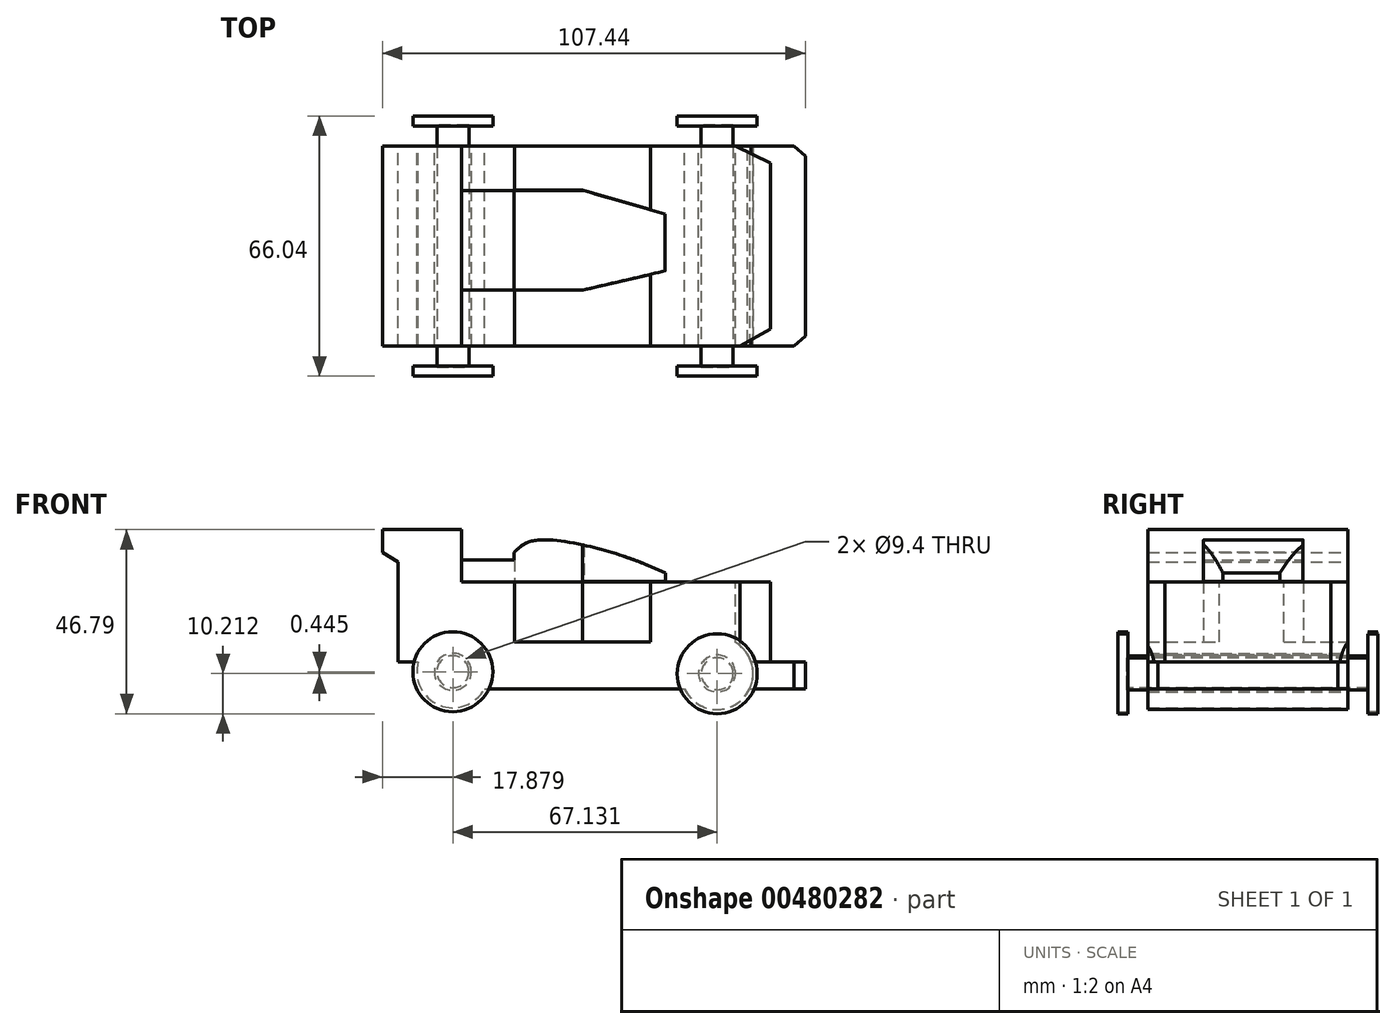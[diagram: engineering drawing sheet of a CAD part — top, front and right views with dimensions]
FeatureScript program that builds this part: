
annotation { "Feature Type Name" : "Feature", "Feature Type Description" : "" }
export const myFeature = defineFeature(function(context is Context, id is Id, definition is map)
    precondition{}
    {
        {
            var Q0;
            Q0=qCreatedBy(makeId("Front.planeOp"),FACE);
            var sketch = newSketch(context, id + "F0", { "sketchPlane" : qUnion([Q0])});
            skCircle(sketch, "E0", {"center": v(-30.53, -30.3) * mm, "radius": 9.14 * mm});
            skPoint(sketch, "E0.first.point", {"position": v(-22.47, -34.62) * mm});
            skPoint(sketch, "E0.second.point", {"position": v(-38.95, -26.72) * mm});
            skPoint(sketch, "E0.third.point", {"position": v(-21.57, -28.46) * mm});
            skCircle(sketch, "E1", {"center": v(36.63, -30.8) * mm, "radius": 9.14 * mm});
            skPoint(sketch, "E1.first.point", {"position": v(27.8, -28.46) * mm});
            skPoint(sketch, "E1.second.point", {"position": v(45.48, -28.46) * mm});
            skPoint(sketch, "E1.third.point", {"position": v(44.94, -34.62) * mm});
            skLineSegment(sketch, "E2", {"start": v(-22.47, -34.62) * mm, "end": v(28.33, -34.62) * mm});
            skLineSegment(sketch, "E3", {"start": v(44.94, -34.62) * mm, "end": v(59.03, -34.62) * mm});
            skLineSegment(sketch, "E4", {"start": v(59.03, -34.62) * mm, "end": v(59.03, -27.76) * mm});
            skLineSegment(sketch, "E5", {"start": v(59.03, -27.76) * mm, "end": v(50.14, -27.76) * mm});
            skLineSegment(sketch, "E6", {"start": v(50.14, -27.76) * mm, "end": v(50.14, -7.44) * mm});
            skLineSegment(sketch, "E7", {"start": v(50.14, -7.44) * mm, "end": v(19.66, -7.44) * mm});
            skLineSegment(sketch, "E8", {"start": v(19.66, -7.44) * mm, "end": v(19.66, -22.68) * mm});
            skLineSegment(sketch, "E9", {"start": v(19.66, -22.68) * mm, "end": v(-14.88, -22.68) * mm});
            skLineSegment(sketch, "E10", {"start": v(-14.88, -22.68) * mm, "end": v(-14.88, -7.44) * mm});
            skLineSegment(sketch, "E11", {"start": v(-14.88, -7.44) * mm, "end": v(-28.34, -7.44) * mm});
            skLineSegment(sketch, "E12", {"start": v(-28.34, -7.44) * mm, "end": v(-28.34, 5.84) * mm});
            skLineSegment(sketch, "E13", {"start": v(-28.34, 5.84) * mm, "end": v(-48.4, 5.84) * mm});
            skLineSegment(sketch, "E14", {"start": v(-48.4, 5.84) * mm, "end": v(-48.4, 0) * mm});
            skLineSegment(sketch, "E15", {"start": v(-48.4, 0) * mm, "end": v(-44.43, -2.36) * mm});
            skLineSegment(sketch, "E16", {"start": v(-44.43, -2.36) * mm, "end": v(-44.43, -27.76) * mm});
            skLineSegment(sketch, "E17", {"start": v(-44.43, -27.76) * mm, "end": v(-38.95, -27.76) * mm});
            skSolve(sketch);
        }
        {
            var Q0;
            Q0=qSketchRegion(id+"F0",true);
            extrude(context, id + "F1", {"entities" : qUnion([Q0]), "depth" : 50.8 * mm});
        }
        {
            var Q0;
            Q0=makeQuery(id+"F1.opExtrude","CAP_FACE",FACE,{"disambiguationData":[OSD([sQuery(id+"F0.wireOp",EDGE,"E0"),sQuery(id+"F0.wireOp",EDGE,"E1"),sQuery(id+"F0.wireOp",EDGE,"E2"),sQuery(id+"F0.wireOp",EDGE,"E3"),sQuery(id+"F0.wireOp",EDGE,"E4"),sQuery(id+"F0.wireOp",EDGE,"E5"),sQuery(id+"F0.wireOp",EDGE,"E6"),sQuery(id+"F0.wireOp",EDGE,"E7"),sQuery(id+"F0.wireOp",EDGE,"E8"),sQuery(id+"F0.wireOp",EDGE,"E9"),sQuery(id+"F0.wireOp",EDGE,"E10"),sQuery(id+"F0.wireOp",EDGE,"E11"),sQuery(id+"F0.wireOp",EDGE,"E12"),sQuery(id+"F0.wireOp",EDGE,"E13"),sQuery(id+"F0.wireOp",EDGE,"E14"),sQuery(id+"F0.wireOp",EDGE,"E15"),sQuery(id+"F0.wireOp",EDGE,"E16"),sQuery(id+"F0.wireOp",EDGE,"E17")])],"isStart":false});
            var sketch = newSketch(context, id + "F2", { "sketchPlane" : qUnion([Q0])});
            skCircle(sketch, "E18", {"center": v(-30.53, -30.3) * mm, "radius": 9.14 * mm});
            skCircle(sketch, "E19", {"center": v(36.63, -30.8) * mm, "radius": 9.14 * mm});
            skSolve(sketch);
        }
        {
            var Q0;
            Q0=qSketchRegion(id+"F2",true);
            extrude(context, id + "F3", {"entities" : qUnion([Q0]), "operationType" : NewBodyOperationType.REMOVE, "oppositeDirection" : true, "depth" : 54.86 * mm});
        }
        {
            var Q0;
            Q0=makeQuery(id+"F1.opExtrude","CAP_FACE",FACE,{"disambiguationData":[OSD([sQuery(id+"F0.wireOp",EDGE,"E0"),sQuery(id+"F0.wireOp",EDGE,"E1"),sQuery(id+"F0.wireOp",EDGE,"E2"),sQuery(id+"F0.wireOp",EDGE,"E3"),sQuery(id+"F0.wireOp",EDGE,"E4"),sQuery(id+"F0.wireOp",EDGE,"E5"),sQuery(id+"F0.wireOp",EDGE,"E6"),sQuery(id+"F0.wireOp",EDGE,"E7"),sQuery(id+"F0.wireOp",EDGE,"E8"),sQuery(id+"F0.wireOp",EDGE,"E9"),sQuery(id+"F0.wireOp",EDGE,"E10"),sQuery(id+"F0.wireOp",EDGE,"E11"),sQuery(id+"F0.wireOp",EDGE,"E12"),sQuery(id+"F0.wireOp",EDGE,"E13"),sQuery(id+"F0.wireOp",EDGE,"E14"),sQuery(id+"F0.wireOp",EDGE,"E15"),sQuery(id+"F0.wireOp",EDGE,"E16"),sQuery(id+"F0.wireOp",EDGE,"E17")])],"isStart":false});
            var sketch = newSketch(context, id + "F4", { "sketchPlane" : qUnion([Q0])});
            skCircle(sketch, "E20", {"center": v(36.63, -30.8) * mm, "radius": 4.06 * mm});
            skCircle(sketch, "E21", {"center": v(-30.53, -30.3) * mm, "radius": 4.06 * mm});
            skSolve(sketch);
        }
        {
            var Q0;
            Q0=qSketchRegion(id+"F4",true);
            extrude(context, id + "F5", {"entities" : qUnion([Q0]), "oppositeDirection" : true, "depth" : 56.13 * mm, "hasSecondDirection" : true, "secondDirectionOppositeDirection" : false, "secondDirectionDepth" : 5.33 * mm});
        }
        {
            var Q0;
            Q0=makeQuery(id+"F1.opExtrude","CAP_FACE",FACE,{"disambiguationData":[OSD([sQuery(id+"F0.wireOp",EDGE,"E0"),sQuery(id+"F0.wireOp",EDGE,"E1"),sQuery(id+"F0.wireOp",EDGE,"E2"),sQuery(id+"F0.wireOp",EDGE,"E3"),sQuery(id+"F0.wireOp",EDGE,"E4"),sQuery(id+"F0.wireOp",EDGE,"E5"),sQuery(id+"F0.wireOp",EDGE,"E6"),sQuery(id+"F0.wireOp",EDGE,"E7"),sQuery(id+"F0.wireOp",EDGE,"E8"),sQuery(id+"F0.wireOp",EDGE,"E9"),sQuery(id+"F0.wireOp",EDGE,"E10"),sQuery(id+"F0.wireOp",EDGE,"E11"),sQuery(id+"F0.wireOp",EDGE,"E12"),sQuery(id+"F0.wireOp",EDGE,"E13"),sQuery(id+"F0.wireOp",EDGE,"E14"),sQuery(id+"F0.wireOp",EDGE,"E15"),sQuery(id+"F0.wireOp",EDGE,"E16"),sQuery(id+"F0.wireOp",EDGE,"E17")])],"isStart":false});
            var sketch = newSketch(context, id + "F6", { "sketchPlane" : qUnion([Q0])});
            skCircle(sketch, "E22", {"center": v(-30.53, -30.3) * mm, "radius": 10.16 * mm});
            skCircle(sketch, "E23", {"center": v(36.63, -30.8) * mm, "radius": 10.16 * mm});
            skSolve(sketch);
        }
        {
            var Q0;
            Q0=qSketchRegion(id+"F6",true);
            extrude(context, id + "F7", {"entities" : qUnion([Q0]), "depth" : 7.62 * mm, "hasSecondDirection" : true, "secondDirectionOppositeDirection" : false, "secondDirectionDepth" : 5.08 * mm});
        }
        {
            var Q0;
            Q0=makeQuery(id+"F1.opExtrude","CAP_FACE",FACE,{"disambiguationData":[OSD([sQuery(id+"F0.wireOp",EDGE,"E0"),sQuery(id+"F0.wireOp",EDGE,"E1"),sQuery(id+"F0.wireOp",EDGE,"E2"),sQuery(id+"F0.wireOp",EDGE,"E3"),sQuery(id+"F0.wireOp",EDGE,"E4"),sQuery(id+"F0.wireOp",EDGE,"E5"),sQuery(id+"F0.wireOp",EDGE,"E6"),sQuery(id+"F0.wireOp",EDGE,"E7"),sQuery(id+"F0.wireOp",EDGE,"E8"),sQuery(id+"F0.wireOp",EDGE,"E9"),sQuery(id+"F0.wireOp",EDGE,"E10"),sQuery(id+"F0.wireOp",EDGE,"E11"),sQuery(id+"F0.wireOp",EDGE,"E12"),sQuery(id+"F0.wireOp",EDGE,"E13"),sQuery(id+"F0.wireOp",EDGE,"E14"),sQuery(id+"F0.wireOp",EDGE,"E15"),sQuery(id+"F0.wireOp",EDGE,"E16"),sQuery(id+"F0.wireOp",EDGE,"E17")])],"isStart":true});
            var sketch = newSketch(context, id + "F8", { "sketchPlane" : qUnion([Q0])});
            skCircle(sketch, "E24", {"center": v(-36.63, -30.8) * mm, "radius": 10.16 * mm});
            skCircle(sketch, "E25", {"center": v(30.53, -30.3) * mm, "radius": 10.16 * mm});
            skSolve(sketch);
        }
        {
            var Q0;
            Q0=qSketchRegion(id+"F8",true);
            extrude(context, id + "F9", {"entities" : qUnion([Q0]), "depth" : 7.62 * mm, "hasSecondDirection" : true, "secondDirectionOppositeDirection" : false, "secondDirectionDepth" : 5.08 * mm});
        }
        {
            var Q0;
            Q0=makeQuery(id+"F1.opExtrude","SWEPT_FACE",FACE,{"disambiguationData":[OSD([sQuery(id+"F0.wireOp",EDGE,"E9")])]});
            var sketch = newSketch(context, id + "F10", { "sketchPlane" : qUnion([Q0])});
            skLineSegment(sketch, "E26.bottom", {"start": v(-14.88, -11.2) * mm, "end": v(19.66, -11.2) * mm});
            skLineSegment(sketch, "E26.top", {"start": v(-14.88, -36.6) * mm, "end": v(19.66, -36.6) * mm});
            skLineSegment(sketch, "E26.left", {"start": v(-14.88, -11.2) * mm, "end": v(-14.88, -36.6) * mm});
            skLineSegment(sketch, "E26.right", {"start": v(19.66, -11.2) * mm, "end": v(19.66, -36.6) * mm});
            skSolve(sketch);
        }
        {
            var Q0;
            Q0=qSketchRegion(id+"F10",true);
            extrude(context, id + "F11", {"entities" : qUnion([Q0]), "operationType" : NewBodyOperationType.ADD, "depth" : 15.24 * mm});
        }
        {
            var Q0;
            Q0=makeQuery(id+"F11.boolean.opBoolean","MERGE",FACE,{"derivedFrom":[makeQuery(id+"F1.opExtrude","SWEPT_FACE",FACE,{"disambiguationData":[OSD([sQuery(id+"F0.wireOp",EDGE,"E7")])]}),makeQuery(id+"F1.opExtrude","SWEPT_FACE",FACE,{"disambiguationData":[OSD([sQuery(id+"F0.wireOp",EDGE,"E11")])]}),makeQuery(id+"F11.opExtrude","CAP_FACE",FACE,{"disambiguationData":[OSD([sQuery(id+"F10.wireOp",EDGE,"E26.bottom"),sQuery(id+"F10.wireOp",EDGE,"E26.top"),sQuery(id+"F10.wireOp",EDGE,"E26.left"),sQuery(id+"F10.wireOp",EDGE,"E26.right")])],"isStart":false})]});
            var sketch = newSketch(context, id + "F12", { "sketchPlane" : qUnion([Q0])});
            skLineSegment(sketch, "E27.bottom", {"start": v(-28.34, -11.32) * mm, "end": v(-14.88, -11.32) * mm});
            skLineSegment(sketch, "E27.top", {"start": v(-28.34, -36.6) * mm, "end": v(-14.88, -36.6) * mm});
            skLineSegment(sketch, "E27.left", {"start": v(-28.34, -11.32) * mm, "end": v(-28.34, -36.6) * mm});
            skLineSegment(sketch, "E27.right", {"start": v(-14.88, -11.32) * mm, "end": v(-14.88, -36.6) * mm});
            skSolve(sketch);
        }
        {
            var Q0;
            Q0=qSketchRegion(id+"F12",true);
            extrude(context, id + "F13", {"entities" : qUnion([Q0]), "operationType" : NewBodyOperationType.ADD, "depth" : 5.6 * mm});
        }
        {
            var Q0;
            Q0=makeQuery(id+"F11.opExtrude","SWEPT_FACE",FACE,{"disambiguationData":[OSD([sQuery(id+"F10.wireOp",EDGE,"E26.top")])]});
            var sketch = newSketch(context, id + "F14", { "sketchPlane" : qUnion([Q0])});
            skFitSpline(sketch, "E28", {"points": [v(-14.95, 0) * mm, v(-9.97, 3.02) * mm, v(9.97, 0) * mm, v(21.32, -4.26) * mm, v(28.47, -7.34) * mm], "startDerivative": vector(20.38, 20.97) * mm, "endDerivative": vector(33.05, -14.25) * mm});
            skLineSegment(sketch, "E29", {"start": v(28.47, -7.34) * mm, "end": v(-14.88, -7.44) * mm});
            skLineSegment(sketch, "E30", {"start": v(-14.88, -7.44) * mm, "end": v(-14.95, 0) * mm});
            skSolve(sketch);
        }
        {
            var Q0;
            Q0=qSketchRegion(id+"F14",true);
            extrude(context, id + "F15", {"entities" : qUnion([Q0]), "operationType" : NewBodyOperationType.ADD, "oppositeDirection" : true, "depth" : 25.27 * mm});
        }
        {
            var Q0;
            {var subQ0=sQuery(id+"F10.wireOp",EDGE,"E26.top");var subQ1=sQuery(id+"F10.wireOp",EDGE,"E26.bottom");var subQ2=makeQuery(id+"F11.opExtrude","CAP_FACE",FACE,{"disambiguationData":[OSD([subQ1,subQ0,sQuery(id+"F10.wireOp",EDGE,"E26.left"),sQuery(id+"F10.wireOp",EDGE,"E26.right")])],"isStart":false});var subQ3=sQuery(id+"F0.wireOp",EDGE,"E6");var subQ4=sQuery(id+"F0.wireOp",EDGE,"E12");var subQ5=sQuery(id+"F0.wireOp",EDGE,"E8");var subQ6=sQuery(id+"F0.wireOp",EDGE,"E10");var subQ7=sQuery(id+"F0.wireOp",EDGE,"E17");var subQ8=sQuery(id+"F0.wireOp",EDGE,"E16");var subQ9=sQuery(id+"F0.wireOp",EDGE,"E15");var subQ10=sQuery(id+"F0.wireOp",EDGE,"E14");var subQ11=sQuery(id+"F0.wireOp",EDGE,"E13");var subQ12=sQuery(id+"F0.wireOp",EDGE,"E11");var subQ13=sQuery(id+"F0.wireOp",EDGE,"E9");var subQ14=sQuery(id+"F0.wireOp",EDGE,"E7");var subQ15=sQuery(id+"F0.wireOp",EDGE,"E5");var subQ16=sQuery(id+"F0.wireOp",EDGE,"E4");var subQ17=sQuery(id+"F0.wireOp",EDGE,"E3");var subQ18=sQuery(id+"F0.wireOp",EDGE,"E2");var subQ19=sQuery(id+"F0.wireOp",EDGE,"E1");var subQ20=sQuery(id+"F0.wireOp",EDGE,"E0");var subQ21=makeQuery(id+"F1.opExtrude","SWEPT_FACE",FACE,{"disambiguationData":[OSD([subQ12])]});var subQ22=makeQuery(id+"F1.opExtrude","SWEPT_FACE",FACE,{"disambiguationData":[OSD([subQ14])]});Q0=makeQuery(id+"F13.boolean.opBoolean","SPLIT",FACE,{"disambiguationData":[TD([makeQuery(id+"F1.opExtrude","CAP_FACE",FACE,{"disambiguationData":[OSD([subQ20,subQ19,subQ18,subQ17,subQ16,subQ15,subQ3,subQ14,subQ5,subQ13,subQ6,subQ12,subQ4,subQ11,subQ10,subQ9,subQ8,subQ7])],"isStart":true}),makeQuery(id+"F1.opExtrude","CAP_FACE",FACE,{"disambiguationData":[OSD([subQ20,subQ19,subQ18,subQ17,subQ16,subQ15,subQ3,subQ14,subQ5,subQ13,subQ6,subQ12,subQ4,subQ11,subQ10,subQ9,subQ8,subQ7])],"isStart":false}),makeQuery(id+"F1.opExtrude","SWEPT_FACE",FACE,{"disambiguationData":[OSD([subQ3])]}),subQ22,makeQuery(id+"F1.opExtrude","SWEPT_FACE",FACE,{"disambiguationData":[OSD([subQ5])]}),makeQuery(id+"F1.opExtrude","SWEPT_FACE",FACE,{"disambiguationData":[OSD([subQ6])]}),subQ21,makeQuery(id+"F1.opExtrude","SWEPT_FACE",FACE,{"disambiguationData":[OSD([subQ4])]}),makeQuery(id+"F11.opExtrude","SWEPT_FACE",FACE,{"disambiguationData":[OSD([subQ1])]}),subQ2,makeQuery(id+"F11.opExtrude","SWEPT_FACE",FACE,{"disambiguationData":[OSD([subQ0])]}),makeQuery(id+"F13.opExtrude","SWEPT_FACE",FACE,{"disambiguationData":[OSD([sQuery(id+"F12.wireOp",EDGE,"E27.bottom")])]}),makeQuery(id+"F13.opExtrude","SWEPT_FACE",FACE,{"disambiguationData":[OSD([sQuery(id+"F12.wireOp",EDGE,"E27.top")])]}),makeQuery(id+"F13.opExtrude","SWEPT_FACE",FACE,{"disambiguationData":[OSD([sQuery(id+"F12.wireOp",EDGE,"E27.right")])]})])],"derivedFrom":makeQuery(id+"F11.boolean.opBoolean","MERGE",FACE,{"derivedFrom":[subQ22,subQ21,subQ2]})});}
            var sketch = newSketch(context, id + "F16", { "sketchPlane" : qUnion([Q0])});
            skLineSegment(sketch, "E31", {"start": v(28.7, -18.8) * mm, "end": v(28.73, -11.19) * mm});
            skLineSegment(sketch, "E32", {"start": v(28.73, -30.45) * mm, "end": v(28.7, -38.07) * mm});
            skLineSegment(sketch, "E33", {"start": v(28.73, -30.45) * mm, "end": v(2.4, -36.6) * mm});
            skLineSegment(sketch, "E34", {"start": v(2.4, -36.6) * mm, "end": v(28.7, -38.07) * mm});
            skLineSegment(sketch, "E35", {"start": v(28.7, -18.8) * mm, "end": v(2.4, -11.2) * mm});
            skLineSegment(sketch, "E36", {"start": v(2.4, -11.2) * mm, "end": v(28.73, -11.19) * mm});
            skSolve(sketch);
        }
        {
            var Q0;
            Q0=qSketchRegion(id+"F16",true);
            extrude(context, id + "F17", {"entities" : qUnion([Q0]), "operationType" : NewBodyOperationType.REMOVE, "depth" : 9.37 * mm});
        }
        {
            var Q0;
            {var subQ0=sQuery(id+"F10.wireOp",EDGE,"E26.top");var subQ1=sQuery(id+"F10.wireOp",EDGE,"E26.bottom");var subQ2=makeQuery(id+"F11.opExtrude","CAP_FACE",FACE,{"disambiguationData":[OSD([subQ1,subQ0,sQuery(id+"F10.wireOp",EDGE,"E26.left"),sQuery(id+"F10.wireOp",EDGE,"E26.right")])],"isStart":false});var subQ3=sQuery(id+"F0.wireOp",EDGE,"E6");var subQ4=sQuery(id+"F0.wireOp",EDGE,"E12");var subQ5=sQuery(id+"F0.wireOp",EDGE,"E8");var subQ6=sQuery(id+"F0.wireOp",EDGE,"E10");var subQ7=sQuery(id+"F0.wireOp",EDGE,"E17");var subQ8=sQuery(id+"F0.wireOp",EDGE,"E16");var subQ9=sQuery(id+"F0.wireOp",EDGE,"E15");var subQ10=sQuery(id+"F0.wireOp",EDGE,"E14");var subQ11=sQuery(id+"F0.wireOp",EDGE,"E13");var subQ12=sQuery(id+"F0.wireOp",EDGE,"E11");var subQ13=sQuery(id+"F0.wireOp",EDGE,"E9");var subQ14=sQuery(id+"F0.wireOp",EDGE,"E7");var subQ15=sQuery(id+"F0.wireOp",EDGE,"E5");var subQ16=sQuery(id+"F0.wireOp",EDGE,"E4");var subQ17=sQuery(id+"F0.wireOp",EDGE,"E3");var subQ18=sQuery(id+"F0.wireOp",EDGE,"E2");var subQ19=sQuery(id+"F0.wireOp",EDGE,"E1");var subQ20=sQuery(id+"F0.wireOp",EDGE,"E0");var subQ21=makeQuery(id+"F1.opExtrude","SWEPT_FACE",FACE,{"disambiguationData":[OSD([subQ12])]});var subQ22=makeQuery(id+"F1.opExtrude","SWEPT_FACE",FACE,{"disambiguationData":[OSD([subQ14])]});Q0=makeQuery(id+"F13.boolean.opBoolean","SPLIT",FACE,{"disambiguationData":[TD([makeQuery(id+"F1.opExtrude","CAP_FACE",FACE,{"disambiguationData":[OSD([subQ20,subQ19,subQ18,subQ17,subQ16,subQ15,subQ3,subQ14,subQ5,subQ13,subQ6,subQ12,subQ4,subQ11,subQ10,subQ9,subQ8,subQ7])],"isStart":true}),makeQuery(id+"F1.opExtrude","CAP_FACE",FACE,{"disambiguationData":[OSD([subQ20,subQ19,subQ18,subQ17,subQ16,subQ15,subQ3,subQ14,subQ5,subQ13,subQ6,subQ12,subQ4,subQ11,subQ10,subQ9,subQ8,subQ7])],"isStart":false}),makeQuery(id+"F1.opExtrude","SWEPT_FACE",FACE,{"disambiguationData":[OSD([subQ3])]}),subQ22,makeQuery(id+"F1.opExtrude","SWEPT_FACE",FACE,{"disambiguationData":[OSD([subQ5])]}),makeQuery(id+"F1.opExtrude","SWEPT_FACE",FACE,{"disambiguationData":[OSD([subQ6])]}),subQ21,makeQuery(id+"F1.opExtrude","SWEPT_FACE",FACE,{"disambiguationData":[OSD([subQ4])]}),makeQuery(id+"F11.opExtrude","SWEPT_FACE",FACE,{"disambiguationData":[OSD([subQ1])]}),subQ2,makeQuery(id+"F11.opExtrude","SWEPT_FACE",FACE,{"disambiguationData":[OSD([subQ0])]}),makeQuery(id+"F13.opExtrude","SWEPT_FACE",FACE,{"disambiguationData":[OSD([sQuery(id+"F12.wireOp",EDGE,"E27.bottom")])]}),makeQuery(id+"F13.opExtrude","SWEPT_FACE",FACE,{"disambiguationData":[OSD([sQuery(id+"F12.wireOp",EDGE,"E27.top")])]}),makeQuery(id+"F13.opExtrude","SWEPT_FACE",FACE,{"disambiguationData":[OSD([sQuery(id+"F12.wireOp",EDGE,"E27.right")])]})])],"derivedFrom":makeQuery(id+"F11.boolean.opBoolean","MERGE",FACE,{"derivedFrom":[subQ22,subQ21,subQ2]})});}
            var sketch = newSketch(context, id + "F18", { "sketchPlane" : qUnion([Q0])});
            skLineSegment(sketch, "E37", {"start": v(50.14, 0) * mm, "end": v(41.25, 0) * mm});
            skLineSegment(sketch, "E38", {"start": v(41.25, 0) * mm, "end": v(50.14, -4.32) * mm});
            skLineSegment(sketch, "E39", {"start": v(50.14, -4.32) * mm, "end": v(50.14, 0) * mm});
            skLineSegment(sketch, "E40", {"start": v(50.14, -50.8) * mm, "end": v(42.37, -50.8) * mm});
            skLineSegment(sketch, "E41", {"start": v(42.37, -50.8) * mm, "end": v(50.14, -46.48) * mm});
            skLineSegment(sketch, "E42", {"start": v(50.14, -46.48) * mm, "end": v(50.14, -50.8) * mm});
            skSolve(sketch);
        }
        {
            var Q0;
            Q0=qSketchRegion(id+"F18",true);
            extrude(context, id + "F19", {"entities" : qUnion([Q0]), "operationType" : NewBodyOperationType.REMOVE, "oppositeDirection" : true, "depth" : 20.32 * mm});
        }
        {
            var Q0;
            {var subQ0=sQuery(id+"F0.wireOp",EDGE,"E15");var subQ1=sQuery(id+"F0.wireOp",EDGE,"E14");var subQ2=sQuery(id+"F0.wireOp",EDGE,"E12");var subQ3=sQuery(id+"F0.wireOp",EDGE,"E11");var subQ4=sQuery(id+"F0.wireOp",EDGE,"E10");var subQ5=sQuery(id+"F0.wireOp",EDGE,"E13");var subQ6=sQuery(id+"F0.wireOp",EDGE,"E2");var subQ7=sQuery(id+"F0.wireOp",EDGE,"E7");var subQ8=sQuery(id+"F0.wireOp",EDGE,"E8");var subQ9=sQuery(id+"F0.wireOp",EDGE,"E9");var subQ10=sQuery(id+"F0.wireOp",EDGE,"E16");var subQ11=sQuery(id+"F0.wireOp",EDGE,"E17");Q0=makeQuery(id+"F19.boolean.opBoolean","SPLIT",FACE,{"disambiguationData":[TD([makeQuery(id+"F1.opExtrude","SWEPT_FACE",FACE,{"disambiguationData":[OSD([subQ6])]})])],"derivedFrom":makeQuery(id+"F1.opExtrude","CAP_FACE",FACE,{"disambiguationData":[OSD([sQuery(id+"F0.wireOp",EDGE,"E0"),sQuery(id+"F0.wireOp",EDGE,"E1"),subQ6,sQuery(id+"F0.wireOp",EDGE,"E3"),sQuery(id+"F0.wireOp",EDGE,"E4"),sQuery(id+"F0.wireOp",EDGE,"E5"),sQuery(id+"F0.wireOp",EDGE,"E6"),subQ7,subQ8,subQ9,subQ4,subQ3,subQ2,subQ5,subQ1,subQ0,subQ10,subQ11])],"isStart":true})});}
            var sketch = newSketch(context, id + "F20", { "sketchPlane" : qUnion([Q0])});
            skCircle(sketch, "E43", {"center": v(30.53, -30.3) * mm, "radius": 9.14 * mm});
            skPoint(sketch, "E43.first.point", {"position": v(39.32, -27.76) * mm});
            skPoint(sketch, "E43.second.point", {"position": v(33.47, -21.64) * mm});
            skPoint(sketch, "E43.third.point", {"position": v(22.47, -34.62) * mm});
            skCircle(sketch, "E44.0", {"center": v(30.53, -30.3) * mm, "radius": 4.7 * mm});
            skCircle(sketch, "E45", {"center": v(-36.6, -30.74) * mm, "radius": 9.14 * mm});
            skCircle(sketch, "E46.0", {"center": v(-36.6, -30.74) * mm, "radius": 4.7 * mm});
            skSolve(sketch);
        }
        {
            var Q0;
            Q0=qSketchRegion(id+"F20",true);
            extrude(context, id + "F21", {"entities" : qUnion([Q0]), "operationType" : NewBodyOperationType.ADD, "oppositeDirection" : true, "depth" : 50.8 * mm});
        }
        {
            var Q0;
            {var subQ0=sQuery(id+"F10.wireOp",EDGE,"E26.top");var subQ1=sQuery(id+"F10.wireOp",EDGE,"E26.bottom");var subQ2=makeQuery(id+"F11.opExtrude","CAP_FACE",FACE,{"disambiguationData":[OSD([subQ1,subQ0,sQuery(id+"F10.wireOp",EDGE,"E26.left"),sQuery(id+"F10.wireOp",EDGE,"E26.right")])],"isStart":false});var subQ3=sQuery(id+"F0.wireOp",EDGE,"E6");var subQ4=sQuery(id+"F0.wireOp",EDGE,"E12");var subQ5=sQuery(id+"F0.wireOp",EDGE,"E8");var subQ6=sQuery(id+"F0.wireOp",EDGE,"E10");var subQ7=sQuery(id+"F0.wireOp",EDGE,"E17");var subQ8=sQuery(id+"F0.wireOp",EDGE,"E16");var subQ9=sQuery(id+"F0.wireOp",EDGE,"E15");var subQ10=sQuery(id+"F0.wireOp",EDGE,"E14");var subQ11=sQuery(id+"F0.wireOp",EDGE,"E13");var subQ12=sQuery(id+"F0.wireOp",EDGE,"E11");var subQ13=sQuery(id+"F0.wireOp",EDGE,"E9");var subQ14=sQuery(id+"F0.wireOp",EDGE,"E7");var subQ15=sQuery(id+"F0.wireOp",EDGE,"E5");var subQ16=sQuery(id+"F0.wireOp",EDGE,"E4");var subQ17=sQuery(id+"F0.wireOp",EDGE,"E3");var subQ18=sQuery(id+"F0.wireOp",EDGE,"E2");var subQ19=sQuery(id+"F0.wireOp",EDGE,"E1");var subQ20=sQuery(id+"F0.wireOp",EDGE,"E0");var subQ21=makeQuery(id+"F1.opExtrude","SWEPT_FACE",FACE,{"disambiguationData":[OSD([subQ12])]});var subQ22=makeQuery(id+"F1.opExtrude","SWEPT_FACE",FACE,{"disambiguationData":[OSD([subQ14])]});Q0=makeQuery(id+"F13.boolean.opBoolean","SPLIT",FACE,{"disambiguationData":[TD([makeQuery(id+"F1.opExtrude","CAP_FACE",FACE,{"disambiguationData":[OSD([subQ20,subQ19,subQ18,subQ17,subQ16,subQ15,subQ3,subQ14,subQ5,subQ13,subQ6,subQ12,subQ4,subQ11,subQ10,subQ9,subQ8,subQ7])],"isStart":true}),makeQuery(id+"F1.opExtrude","CAP_FACE",FACE,{"disambiguationData":[OSD([subQ20,subQ19,subQ18,subQ17,subQ16,subQ15,subQ3,subQ14,subQ5,subQ13,subQ6,subQ12,subQ4,subQ11,subQ10,subQ9,subQ8,subQ7])],"isStart":false}),makeQuery(id+"F1.opExtrude","SWEPT_FACE",FACE,{"disambiguationData":[OSD([subQ3])]}),subQ22,makeQuery(id+"F1.opExtrude","SWEPT_FACE",FACE,{"disambiguationData":[OSD([subQ5])]}),makeQuery(id+"F1.opExtrude","SWEPT_FACE",FACE,{"disambiguationData":[OSD([subQ6])]}),subQ21,makeQuery(id+"F1.opExtrude","SWEPT_FACE",FACE,{"disambiguationData":[OSD([subQ4])]}),makeQuery(id+"F11.opExtrude","SWEPT_FACE",FACE,{"disambiguationData":[OSD([subQ1])]}),subQ2,makeQuery(id+"F11.opExtrude","SWEPT_FACE",FACE,{"disambiguationData":[OSD([subQ0])]}),makeQuery(id+"F13.opExtrude","SWEPT_FACE",FACE,{"disambiguationData":[OSD([sQuery(id+"F12.wireOp",EDGE,"E27.bottom")])]}),makeQuery(id+"F13.opExtrude","SWEPT_FACE",FACE,{"disambiguationData":[OSD([sQuery(id+"F12.wireOp",EDGE,"E27.top")])]}),makeQuery(id+"F13.opExtrude","SWEPT_FACE",FACE,{"disambiguationData":[OSD([sQuery(id+"F12.wireOp",EDGE,"E27.right")])]})])],"derivedFrom":makeQuery(id+"F11.boolean.opBoolean","MERGE",FACE,{"derivedFrom":[subQ22,subQ21,subQ2]})});}
            var sketch = newSketch(context, id + "F22", { "sketchPlane" : qUnion([Q0])});
            skLineSegment(sketch, "E47.bottom", {"start": v(23.35, -17.23) * mm, "end": v(30.33, -17.23) * mm});
            skLineSegment(sketch, "E47.top", {"start": v(23.35, -31.67) * mm, "end": v(30.33, -31.67) * mm});
            skLineSegment(sketch, "E47.left", {"start": v(23.35, -17.23) * mm, "end": v(23.35, -31.67) * mm});
            skLineSegment(sketch, "E47.right", {"start": v(30.33, -17.23) * mm, "end": v(30.33, -31.67) * mm});
            skSolve(sketch);
        }
        {
            var Q0;
            Q0=qSketchRegion(id+"F22",true);
            extrude(context, id + "F23", {"entities" : qUnion([Q0]), "operationType" : NewBodyOperationType.REMOVE, "depth" : 11.18 * mm});
        }
        {
            var Q0;
            Q0=makeQuery(id+"F19.boolean.opBoolean","MERGE",FACE,{"derivedFrom":[makeQuery(id+"F1.opExtrude","SWEPT_FACE",FACE,{"disambiguationData":[OSD([sQuery(id+"F0.wireOp",EDGE,"E5")])]}),makeQuery(id+"F19.opExtrude","CAP_FACE",FACE,{"disambiguationData":[OSD([sQuery(id+"F18.wireOp",EDGE,"E37"),sQuery(id+"F18.wireOp",EDGE,"E38"),sQuery(id+"F18.wireOp",EDGE,"E39")])],"isStart":false}),makeQuery(id+"F19.opExtrude","CAP_FACE",FACE,{"disambiguationData":[OSD([sQuery(id+"F18.wireOp",EDGE,"E40"),sQuery(id+"F18.wireOp",EDGE,"E41"),sQuery(id+"F18.wireOp",EDGE,"E42")])],"isStart":false})]});
            var sketch = newSketch(context, id + "F24", { "sketchPlane" : qUnion([Q0])});
            skLineSegment(sketch, "E48", {"start": v(56.14, 0) * mm, "end": v(59.03, -2.55) * mm});
            skLineSegment(sketch, "E49", {"start": v(59.03, 0) * mm, "end": v(56.14, 0) * mm});
            skLineSegment(sketch, "E50", {"start": v(56.15, -50.8) * mm, "end": v(59.03, -48.23) * mm});
            skLineSegment(sketch, "E51", {"start": v(59.03, -48.23) * mm, "end": v(59.03, -50.8) * mm});
            skLineSegment(sketch, "E52", {"start": v(59.03, -2.55) * mm, "end": v(59.03, 0) * mm});
            skLineSegment(sketch, "E53", {"start": v(56.15, -50.8) * mm, "end": v(59.03, -50.8) * mm});
            skSolve(sketch);
        }
        {
            var Q0;
            Q0=qSketchRegion(id+"F24",true);
            extrude(context, id + "F25", {"entities" : qUnion([Q0]), "operationType" : NewBodyOperationType.REMOVE, "oppositeDirection" : true, "depth" : 25.4 * mm});
        }
        {
            var Q0;
            {var subQ0=sQuery(id+"F10.wireOp",EDGE,"E26.top");var subQ1=sQuery(id+"F10.wireOp",EDGE,"E26.bottom");var subQ2=makeQuery(id+"F11.opExtrude","CAP_FACE",FACE,{"disambiguationData":[OSD([subQ1,subQ0,sQuery(id+"F10.wireOp",EDGE,"E26.left"),sQuery(id+"F10.wireOp",EDGE,"E26.right")])],"isStart":false});var subQ3=sQuery(id+"F0.wireOp",EDGE,"E6");var subQ4=sQuery(id+"F0.wireOp",EDGE,"E12");var subQ5=sQuery(id+"F0.wireOp",EDGE,"E8");var subQ6=sQuery(id+"F0.wireOp",EDGE,"E10");var subQ7=sQuery(id+"F0.wireOp",EDGE,"E17");var subQ8=sQuery(id+"F0.wireOp",EDGE,"E16");var subQ9=sQuery(id+"F0.wireOp",EDGE,"E15");var subQ10=sQuery(id+"F0.wireOp",EDGE,"E14");var subQ11=sQuery(id+"F0.wireOp",EDGE,"E13");var subQ12=sQuery(id+"F0.wireOp",EDGE,"E11");var subQ13=sQuery(id+"F0.wireOp",EDGE,"E9");var subQ14=sQuery(id+"F0.wireOp",EDGE,"E7");var subQ15=sQuery(id+"F0.wireOp",EDGE,"E5");var subQ16=sQuery(id+"F0.wireOp",EDGE,"E4");var subQ17=sQuery(id+"F0.wireOp",EDGE,"E3");var subQ18=sQuery(id+"F0.wireOp",EDGE,"E2");var subQ19=sQuery(id+"F0.wireOp",EDGE,"E1");var subQ20=sQuery(id+"F0.wireOp",EDGE,"E0");var subQ21=makeQuery(id+"F1.opExtrude","SWEPT_FACE",FACE,{"disambiguationData":[OSD([subQ12])]});var subQ22=makeQuery(id+"F1.opExtrude","SWEPT_FACE",FACE,{"disambiguationData":[OSD([subQ14])]});Q0=makeQuery(id+"F13.boolean.opBoolean","SPLIT",FACE,{"disambiguationData":[TD([makeQuery(id+"F1.opExtrude","CAP_FACE",FACE,{"disambiguationData":[OSD([subQ20,subQ19,subQ18,subQ17,subQ16,subQ15,subQ3,subQ14,subQ5,subQ13,subQ6,subQ12,subQ4,subQ11,subQ10,subQ9,subQ8,subQ7])],"isStart":true}),makeQuery(id+"F1.opExtrude","CAP_FACE",FACE,{"disambiguationData":[OSD([subQ20,subQ19,subQ18,subQ17,subQ16,subQ15,subQ3,subQ14,subQ5,subQ13,subQ6,subQ12,subQ4,subQ11,subQ10,subQ9,subQ8,subQ7])],"isStart":false}),makeQuery(id+"F1.opExtrude","SWEPT_FACE",FACE,{"disambiguationData":[OSD([subQ3])]}),subQ22,makeQuery(id+"F1.opExtrude","SWEPT_FACE",FACE,{"disambiguationData":[OSD([subQ5])]}),makeQuery(id+"F1.opExtrude","SWEPT_FACE",FACE,{"disambiguationData":[OSD([subQ6])]}),subQ21,makeQuery(id+"F1.opExtrude","SWEPT_FACE",FACE,{"disambiguationData":[OSD([subQ4])]}),makeQuery(id+"F11.opExtrude","SWEPT_FACE",FACE,{"disambiguationData":[OSD([subQ1])]}),subQ2,makeQuery(id+"F11.opExtrude","SWEPT_FACE",FACE,{"disambiguationData":[OSD([subQ0])]}),makeQuery(id+"F13.opExtrude","SWEPT_FACE",FACE,{"disambiguationData":[OSD([sQuery(id+"F12.wireOp",EDGE,"E27.bottom")])]}),makeQuery(id+"F13.opExtrude","SWEPT_FACE",FACE,{"disambiguationData":[OSD([sQuery(id+"F12.wireOp",EDGE,"E27.top")])]}),makeQuery(id+"F13.opExtrude","SWEPT_FACE",FACE,{"disambiguationData":[OSD([sQuery(id+"F12.wireOp",EDGE,"E27.right")])]})])],"derivedFrom":makeQuery(id+"F11.boolean.opBoolean","MERGE",FACE,{"derivedFrom":[subQ22,subQ21,subQ2]})});}
            var sketch = newSketch(context, id + "F26", { "sketchPlane" : qUnion([Q0])});
            skLineSegment(sketch, "E54", {"start": v(19.66, -11.2) * mm, "end": v(19.66, -16.17) * mm});
            skLineSegment(sketch, "E55", {"start": v(19.66, -16.17) * mm, "end": v(2.4, -11.2) * mm});
            skLineSegment(sketch, "E56", {"start": v(2.4, -11.2) * mm, "end": v(19.66, -11.2) * mm});
            skLineSegment(sketch, "E57", {"start": v(19.66, -36.6) * mm, "end": v(2.4, -36.6) * mm});
            skLineSegment(sketch, "E58", {"start": v(2.4, -36.6) * mm, "end": v(19.66, -32.59) * mm});
            skLineSegment(sketch, "E59", {"start": v(19.66, -32.59) * mm, "end": v(19.66, -36.6) * mm});
            skSolve(sketch);
        }
        {
            var Q0;
            Q0 = qSketchRegion(id + "F26", true);
            extrude(context, id + "F27", {"entities" : qUnion([Q0]), "operationType" : NewBodyOperationType.REMOVE, "oppositeDirection" : true, "depth" : 15.24 * mm});
        }
    });
